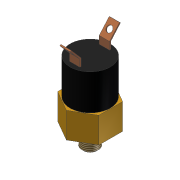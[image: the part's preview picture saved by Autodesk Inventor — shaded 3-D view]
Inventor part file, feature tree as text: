
AUTODESK INVENTOR PART (.ipt)
format: ipt  version: unknown  size: 244,736 bytes
history: native  units: mm (DEFAULTED — no unit token found)
features: extrude x6, sketch x6, projected_geometry x4, mirror x1, thread x1, chamfer x1, fillet x1
ambient origin geometry x8: Origin, YZ Plane, XZ Plane, XY Plane, X Axis, Y Axis, Z Axis, Center Point
feature tree (20):
  extrude  "Extrusion1"  Depth=15.875mm TaperAngle=0.0deg
  extrude  "Extrusion2"  Depth=11.049mm TaperAngle=0.0deg
  extrude  "Extrusion3"  Depth=19.9898mm TaperAngle=0.0deg
  extrude  "Extrusion4"  Depth=21.971mm TaperAngle=0.0deg
  extrude  "Extrusion5"  Depth=0.762mm
  extrude  "Extrusion6"  Depth=4.699mm
  mirror  "Mirror1"
  thread  "Thread1"  [1 undecoded]
  chamfer  "Chamfer1"  Distance=6.35mm
  fillet  "Fillet1"  Radius=6.35mm
  sketch  "Sketch1"  dims[d0=25.4mm d1=15.875mm d2=0.0mm]
  sketch  "Sketch2"  dims[d3=10.16mm d4=11.049mm d5=0.0mm]
  projected_geometry  "Projected Loop1"
  sketch  "Sketch3"  dims[d6=3.175mm d7=19.9898mm d8=0.0mm]
  sketch  "Sketch4"  dims[d9=24.765mm d10=21.971mm d11=0.0mm]
  projected_geometry  "Projected Loop2"
  sketch  "Sketch5"  dims[d12=19.05mm d13=0.762mm]
  projected_geometry  "Projected Loop3"
  sketch  "Sketch6"  dims[d14=0.762mm d15=4.699mm d17=9.398mm d18=6.35mm d19=0.0mm d20=6.35mm d21=0.0mm d22=25.4mm d23=0.0mm d24=1.0mm d25=3.175mm d26=45.0deg d27=3.175mm]
  projected_geometry  "Projected Loop4"
note: 1 required parameter value undecoded (feature->parameter linkage not recoverable at this tier; creation-order binding heuristic only, values carry confidence <= 0.55)
